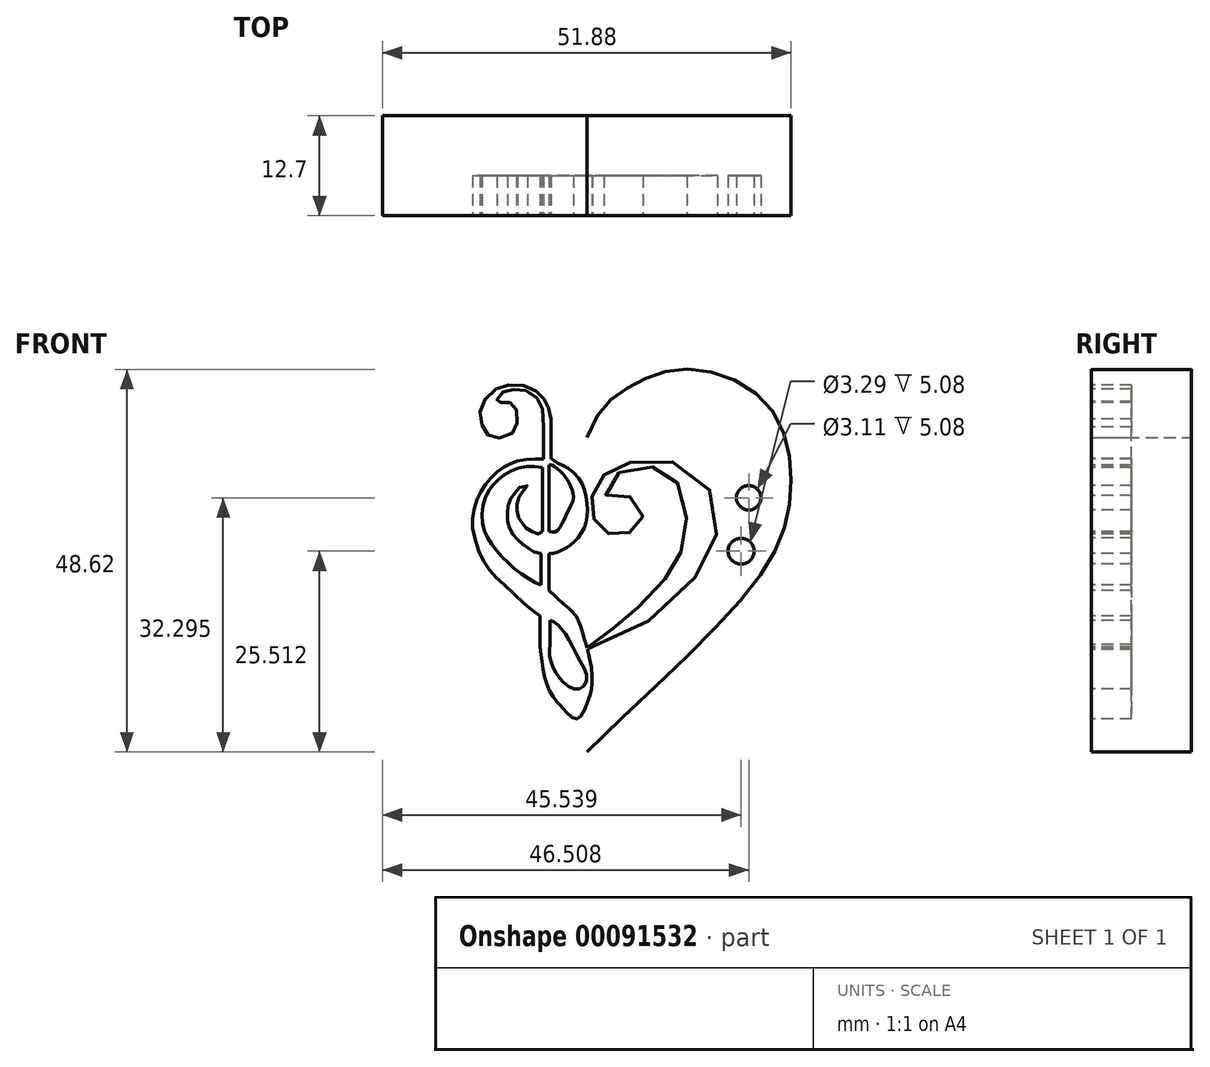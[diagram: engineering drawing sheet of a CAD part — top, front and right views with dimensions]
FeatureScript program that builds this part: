
annotation { "Feature Type Name" : "Feature", "Feature Type Description" : "" }
export const myFeature = defineFeature(function(context is Context, id is Id, definition is map)
    precondition{}
    {
        {
            var Q0;
            Q0=qCreatedBy(makeId("Front.planeOp"),FACE);
            var sketch = newSketch(context, id + "F0", { "sketchPlane" : qUnion([Q0])});
            skFitSpline(sketch, "E0", {"points": [v(0, 39.95) * mm, v(5.45, 46.44) * mm, v(13.46, 48.6) * mm, v(23.18, 43.87) * mm, v(25.92, 33.65) * mm, v(22.18, 22.68) * mm, v(0, 0) * mm], "startDerivative": vector(24.9, 76.21) * mm, "endDerivative": vector(-102.74, -100.55) * mm});
            skLineSegment(sketch, "E1", {"start": v(0, 39.95) * mm, "end": v(0, 0) * mm});
            skFitSpline(sketch, "E2.MirrorCS", {"points": [v(0, 39.95) * mm, v(-5.45, 46.44) * mm, v(-13.46, 48.6) * mm, v(-23.18, 43.87) * mm, v(-25.92, 33.65) * mm, v(-22.18, 22.68) * mm, v(0, 0) * mm], "startDerivative": vector(-24.9, 76.21) * mm, "endDerivative": vector(102.74, -100.55) * mm});
            skSolve(sketch);
        }
        {
            var Q0;
            Q0=qSketchRegion(id+"F0",true);
            extrude(context, id + "F1", {"entities" : qUnion([Q0]), "depth" : 12.7 * mm});
        }
        {
            var Q0;
            Q0=makeQuery(id+"F1.opExtrude","CAP_FACE",FACE,{"disambiguationData":[OSD([sQuery(id+"F0.wireOp",EDGE,"E0"),sQuery(id+"F0.wireOp",EDGE,"E2.MirrorCS")])],"isStart":false});
            var sketch = newSketch(context, id + "F2", { "sketchPlane" : qUnion([Q0])});
            skFitSpline(sketch, "E3", {"points": [v(3.32, 32.59) * mm, v(4.68, 32.59) * mm, v(5.7, 32.3) * mm, v(6.62, 31.33) * mm, v(7.1, 30.36) * mm, v(6.97, 29.28) * mm, v(6.42, 28.52) * mm, v(5.65, 27.93) * mm, v(4.68, 27.74) * mm, v(3.8, 27.74) * mm, v(2.84, 27.74) * mm, v(2.06, 28.03) * mm, v(1.22, 28.82) * mm, v(0.9, 29.58) * mm, v(0.7, 30.55) * mm, v(0.7, 31.42) * mm, v(0.7, 32.78) * mm, v(1.19, 34.04) * mm, v(1.96, 35) * mm, v(2.64, 35.59) * mm, v(3.8, 36.27) * mm, v(7.4, 37.14) * mm, v(10.88, 36.85) * mm, v(14.85, 34.33) * mm, v(16.4, 31.04) * mm, v(16.2, 26.29) * mm, v(13.69, 22.12) * mm, v(7.4, 16.4) * mm, v(0, 13.11) * mm, v(1.77, 14.66) * mm, v(3.13, 15.53) * mm, v(4.68, 16.7) * mm, v(6.42, 18.25) * mm, v(8.55, 20.47) * mm, v(10.59, 22.8) * mm, v(11.65, 24.48) * mm, v(12.14, 26.1) * mm, v(12.59, 28.45) * mm, v(12.59, 31.47) * mm, v(11.68, 33.9) * mm, v(10.3, 35.5) * mm, v(8.75, 36.17) * mm, v(6.13, 36.07) * mm, v(4.1, 35.5) * mm, v(2.55, 34.14) * mm, v(2.3, 32.77) * mm, v(3.32, 32.59) * mm]});
            skCircle(sketch, "E4", {"center": v(20.57, 32.3) * mm, "radius": 1.55 * mm});
            skCircle(sketch, "E5", {"center": v(19.6, 25.51) * mm, "radius": 1.65 * mm});
            skLineSegment(sketch, "E6", {"start": v(-5.6, 36.17) * mm, "end": v(-5.6, 28.03) * mm});
            skLineSegment(sketch, "E7", {"start": v(-4.78, 36.47) * mm, "end": v(-4.78, 28.03) * mm});
            skPoint(sketch, "E8.3.internal.snap0", {"position": v(-4.78, 32.25) * mm});
            skFitSpline(sketch, "E8", {"points": [v(-4.78, 28.03) * mm, v(-3.85, 28.03) * mm, v(-2.73, 29.86) * mm, v(-1.72, 32.25) * mm, v(-2.1, 33.84) * mm, v(-2.84, 35.13) * mm, v(-3.97, 36.17) * mm, v(-4.78, 36.47) * mm], "startDerivative": vector(8.2, -1.96) * mm, "endDerivative": vector(-8.43, -2.04) * mm});
            skFitSpline(sketch, "E9", {"points": [v(-5.6, 28.03) * mm, v(-5.89, 27.7) * mm, v(-6.48, 27.77) * mm, v(-7.05, 28.03) * mm, v(-7.63, 28.4) * mm, v(-7.95, 28.73) * mm, v(-8.31, 29.24) * mm, v(-8.75, 29.9) * mm, v(-8.86, 30.66) * mm, v(-8.93, 31.25) * mm, v(-8.75, 31.94) * mm, v(-8.5, 32.62) * mm, v(-7.83, 33.4) * mm, v(-7.56, 33.79) * mm, v(-8.33, 33.72) * mm, v(-8.95, 33.12) * mm, v(-9.48, 32.48) * mm, v(-9.77, 32) * mm, v(-10, 31.2) * mm, v(-10.05, 30.54) * mm, v(-10.07, 29.56) * mm, v(-9.93, 28.87) * mm, v(-9.64, 28.03) * mm, v(-9.27, 27.53) * mm, v(-8.79, 27) * mm, v(-8.33, 26.54) * mm, v(-7.8, 26.17) * mm, v(-7.2, 25.72) * mm, v(-6.53, 25.37) * mm, v(-5.8, 25.24) * mm], "startDerivative": vector(-7.9, -16.06) * mm, "endDerivative": vector(21.06, -2.57) * mm});
            skLineSegment(sketch, "E10", {"start": v(-5.8, 25.24) * mm, "end": v(-5.8, 21.2) * mm});
            skLineSegment(sketch, "E11", {"start": v(-4.82, 25.22) * mm, "end": v(-4.82, 20.54) * mm});
            skLineSegment(sketch, "E12", {"start": v(-5.95, 17.26) * mm, "end": v(-5.95, 13.34) * mm});
            skLineSegment(sketch, "E13", {"start": v(-4.68, 16.72) * mm, "end": v(-4.68, 13.67) * mm});
            skLineSegment(sketch, "E14", {"start": v(-5.5, 37.2) * mm, "end": v(-5.5, 41.31) * mm});
            skLineSegment(sketch, "E15", {"start": v(-4.54, 37.31) * mm, "end": v(-4.54, 42.29) * mm});
            skFitSpline(sketch, "E16", {"points": [v(-4.82, 25.22) * mm, v(-3.65, 25.42) * mm, v(-2.46, 26.03) * mm, v(-1.69, 26.6) * mm, v(-0.51, 28.1) * mm, v(0, 29.65) * mm, v(0, 31.92) * mm, v(-0.67, 34.25) * mm, v(-2.34, 36) * mm, v(-3.97, 36.87) * mm, v(-4.54, 37.31) * mm], "startDerivative": vector(9.27, -1.22) * mm, "endDerivative": vector(-7.22, 6.46) * mm});
            skFitSpline(sketch, "E17", {"points": [v(-5.5, 37.2) * mm, v(-7.04, 37.2) * mm, v(-8.87, 36.98) * mm, v(-9.95, 36.49) * mm, v(-11, 35.9) * mm, v(-12.28, 34.7) * mm, v(-13.15, 33.55) * mm, v(-13.97, 32.07) * mm, v(-14.5, 29.89) * mm, v(-14.44, 28.03) * mm, v(-13.54, 25.13) * mm, v(-12.18, 22.89) * mm, v(-10.43, 21.2) * mm, v(-7.56, 18.52) * mm, v(-5.95, 17.26) * mm], "startDerivative": vector(-23.54, 0.4) * mm, "endDerivative": vector(20.41, -14.95) * mm});
            skFitSpline(sketch, "E18", {"points": [v(-5.8, 21.2) * mm, v(-7.3, 21.96) * mm, v(-9.35, 23.45) * mm, v(-11, 25.1) * mm, v(-12.42, 26.9) * mm, v(-13.1, 28.43) * mm, v(-13.26, 31) * mm, v(-12.38, 33.3) * mm, v(-11.4, 34.43) * mm, v(-9.87, 35.61) * mm, v(-7.8, 36.23) * mm, v(-5.6, 36.17) * mm], "startDerivative": vector(-17.72, 7.98) * mm, "endDerivative": vector(23.64, -2.1) * mm});
            skFitSpline(sketch, "E19", {"points": [v(-5.95, 13.34) * mm, v(-5.55, 10.5) * mm, v(-4.68, 7.67) * mm, v(-3.61, 6.18) * mm, v(-2.73, 5.2) * mm, v(-1.3, 4.18) * mm, v(0, 6.08) * mm, v(0.6, 8.18) * mm, v(0.5, 11.21) * mm, v(-0.67, 15.53) * mm, v(-1.44, 17.37) * mm, v(-3.24, 19.07) * mm, v(-4.82, 20.54) * mm], "startDerivative": vector(3.64, -30.52) * mm, "endDerivative": vector(-18.85, 18.3) * mm});
            skFitSpline(sketch, "E20", {"points": [v(-4.68, 16.72) * mm, v(-3.7, 16.2) * mm, v(-2.52, 14.65) * mm, v(-0.98, 11.83) * mm, v(0, 9.26) * mm, v(-0.98, 8.03) * mm, v(-2.62, 8.54) * mm, v(-3.9, 10.08) * mm, v(-4.68, 11.93) * mm, v(-4.68, 13.67) * mm], "startDerivative": vector(13.4, -4.4) * mm, "endDerivative": vector(2.13, 16.24) * mm});
            skFitSpline(sketch, "E21", {"points": [v(-4.54, 42.29) * mm, v(-4.8, 43.54) * mm, v(-5.2, 44.56) * mm, v(-6, 45.46) * mm, v(-7.25, 46.34) * mm, v(-9.49, 46.63) * mm, v(-11.2, 46.3) * mm, v(-12.93, 44.8) * mm, v(-13.54, 43.1) * mm, v(-13.28, 41.41) * mm, v(-12.52, 40.28) * mm, v(-11.2, 39.9) * mm, v(-9.4, 40.54) * mm, v(-8.88, 41.65) * mm, v(-8.9, 43.36) * mm, v(-9.52, 44.24) * mm, v(-10.28, 44.53) * mm, v(-11.15, 44.38) * mm, v(-11.35, 44.44) * mm, v(-11.41, 44.88) * mm, v(-10.8, 45.64) * mm, v(-9.75, 45.99) * mm, v(-8.32, 46.05) * mm, v(-6.66, 45.29) * mm, v(-5.82, 44.1) * mm, v(-5.5, 41.31) * mm], "startDerivative": vector(-6.7, 29.56) * mm, "endDerivative": vector(-3.25, -66.24) * mm});
            skSolve(sketch);
        }
        {
            var Q0;
            Q0 = qSketchRegion(id + "F2", true);
            extrude(context, id + "F3", {"entities" : qUnion([Q0]), "operationType" : NewBodyOperationType.ADD, "depth" : 25.4 * mm});
        }
        {
            var Q0;
            Q0=makeQuery(id+"F3.opExtrude","CAP_FACE",FACE,{"disambiguationData":[OSD([sQuery(id+"F2.wireOp",EDGE,"E5")])],"isStart":false});
            var Q1;
            Q1=makeQuery(id+"F3.opExtrude","CAP_FACE",FACE,{"disambiguationData":[OSD([sQuery(id+"F2.wireOp",EDGE,"E4")])],"isStart":false});
            var Q2;
            Q2=makeQuery(id+"F3.opExtrude","CAP_FACE",FACE,{"disambiguationData":[OSD([sQuery(id+"F2.wireOp",EDGE,"E3"),sQuery(id+"F2.wireOp",EDGE,"E6"),sQuery(id+"F2.wireOp",EDGE,"E7"),sQuery(id+"F2.wireOp",EDGE,"E8"),sQuery(id+"F2.wireOp",EDGE,"E9"),sQuery(id+"F2.wireOp",EDGE,"E10"),sQuery(id+"F2.wireOp",EDGE,"E11"),sQuery(id+"F2.wireOp",EDGE,"E12"),sQuery(id+"F2.wireOp",EDGE,"E13"),sQuery(id+"F2.wireOp",EDGE,"E14"),sQuery(id+"F2.wireOp",EDGE,"E15"),sQuery(id+"F2.wireOp",EDGE,"E16"),sQuery(id+"F2.wireOp",EDGE,"E17"),sQuery(id+"F2.wireOp",EDGE,"E18"),sQuery(id+"F2.wireOp",EDGE,"E19"),sQuery(id+"F2.wireOp",EDGE,"E20"),sQuery(id+"F2.wireOp",EDGE,"E21")])],"isStart":false});
            extrude(context, id + "F4", {"entities" : qUnion([Q0, Q1, Q2]), "operationType" : NewBodyOperationType.REMOVE, "oppositeDirection" : true, "depth" : 30.48 * mm});
        }
    });
